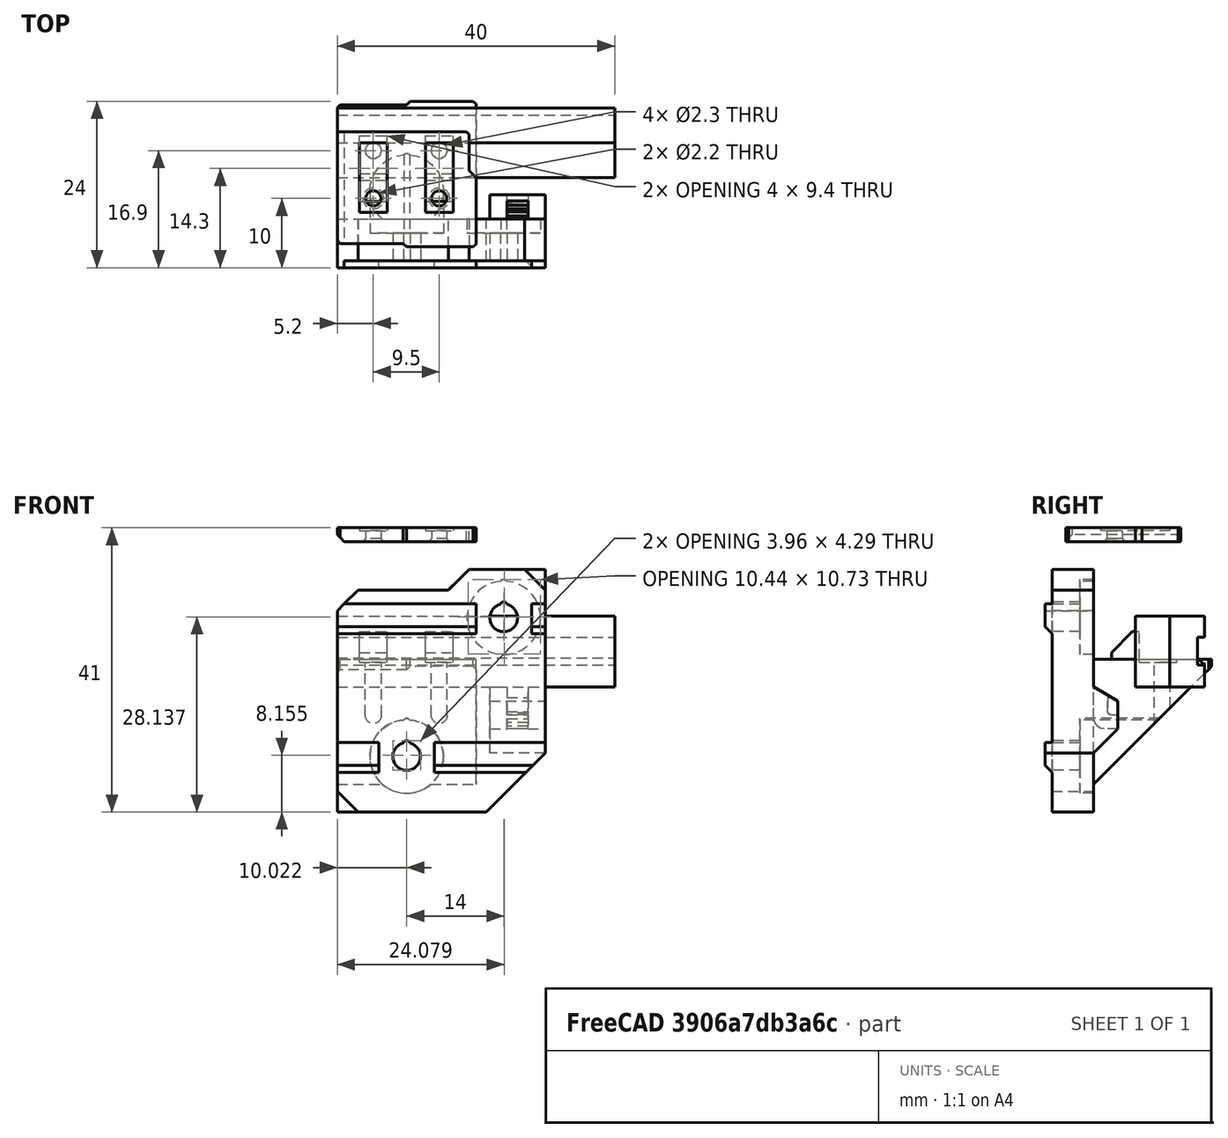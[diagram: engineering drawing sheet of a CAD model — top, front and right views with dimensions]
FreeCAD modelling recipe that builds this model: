
FCSTD DOCUMENT  (FreeCAD 0.18R14555 (Git shallow))
Label: Y-end-stop
License: All rights reserved
LicenseURL: http://en.wikipedia.org/wiki/All_rights_reserved
objects: Part::Cut×21, Part::Box×18, Part::Cylinder×14, Part::Chamfer×12, Part::MultiFuse×11, Part::Feature×10, App::DocumentObjectGroup×1
note: 86 computed .brp shape members not serialized (recipe doc carries the construction recipe); baked Part::Feature solids carry a one-line shape summary decoded from their .brp

FEATURE [Part::Cylinder] Cylinder
  Angle = 360
  AttacherType = Attacher::AttachEngine3D
  Height = 10
  Placement = pos=(5.2,2.9,0) rot=(0,0,1;0rad)
  Radius = 0.9
FEATURE [Part::Cylinder] Cylinder001
  Angle = 360
  AttacherType = Attacher::AttachEngine3D
  Height = 10
  Placement = pos=(14.7,2.9,0) rot=(0,0,1;0rad)
  Radius = 0.9
FEATURE [Part::Box] Box  label="Cube"
  AttacherType = Attacher::AttachEngine3D
  Height = 18
  Length = 10
  Placement = pos=(0,-7,-14) rot=(0,0,1;0rad)
  Width = 16.5
FEATURE [Part::Box] Box001  label="Cube001"
  AttacherType = Attacher::AttachEngine3D
  Height = 18
  Length = 10.5
  Placement = pos=(9.5,-7,-14) rot=(0,0,1;0rad)
  Width = 17
FEATURE [Part::Box] Box002  label="Cube002"
  AttacherType = Attacher::AttachEngine3D
  Height = 0.4
  Length = 4
  Placement = pos=(3.2,-0.4,3.6) rot=(0,0,1;0rad)
  Width = 5.4
FEATURE [Part::Box] Box003  label="Cube003"
  AttacherType = Attacher::AttachEngine3D
  Height = 0.4
  Length = 4
  Placement = pos=(12.7,-0.4,3.6) rot=(0,0,1;0rad)
  Width = 5.4
FEATURE [Part::Box] Box007  label="Cube007"
  AttacherType = Attacher::AttachEngine3D
  Height = 35
  Length = 30
  Placement = pos=(0,-12,-18) rot=(0,0,1;0rad)
  Width = 6
FEATURE [Part::MultiFuse] Fusion003
  Shapes = -> [Box003,Box002]
FEATURE [Part::Cylinder] Cylinder002
  Angle = 360
  AttacherType = Attacher::AttachEngine3D
  Height = 16
  Placement = pos=(10,9,-10) rot=(1,0,0;1.5708rad)
  Radius = 5.3
FEATURE [Part::Chamfer] Chamfer
  Base = -> Box001
  Edges = 1 edges r=1: [Edge3]
FEATURE [Part::Chamfer] Chamfer003
  Base = -> Box
  Edges = 1 edges r=0.4: [Edge3]
FEATURE [Part::Chamfer] Chamfer004
  Base = -> Chamfer
  Edges = 1 edges r=0.4: [Edge15]
FEATURE [Part::MultiFuse] Fusion
  Shapes = -> [Chamfer004,Chamfer003]
FEATURE [Part::Cut] Cut
  Base = -> Fusion
  Tool = -> Fusion003
FEATURE [Part::Feature] Body001
  Placement = pos=(0,-7,5) rot=(0,0,1;0rad)
  shape: bbox 20 x 19 x 19 mm, 5 faces (baked)
FEATURE [Part::Feature] Part__Feature  label="Common002"
  Placement = pos=(44.5,56.745,-30) rot=(0,0,1;3.14159rad)
  shape: bbox 8 x 3.5 x 9.5 mm, 30 faces (baked)
FEATURE [Part::Cylinder] Cylinder004
  Angle = 360
  AttacherType = Attacher::AttachEngine3D
  Height = 16
  Placement = pos=(24,9,10) rot=(1,0,0;1.5708rad)
  Radius = 5.3
FEATURE [Part::Feature] Fusion008001  label="Fusion009"
  shape: bbox 30 x 1.4 x 8.45 mm, 8 faces (baked)
FEATURE [Part::Feature] Fusion008002  label="Fusion010"
  Placement = pos=(0,0,20) rot=(0,0,1;0rad)
  shape: bbox 30 x 1.4 x 8.45 mm, 8 faces (baked)
FEATURE [Part::MultiFuse] Fusion008005
  Placement = pos=(0,0,-5) rot=(0,0,1;0rad)
  Shapes = -> [Cylinder001,Cylinder]
FEATURE [Part::Cylinder] Cylinder005
  Angle = 360
  AttacherType = Attacher::AttachEngine3D
  Height = 25
  Placement = pos=(24,9,10) rot=(1,0,0;1.5708rad)
  Radius = 2
FEATURE [Part::Cylinder] Cylinder006
  Angle = 360
  AttacherType = Attacher::AttachEngine3D
  Height = 25
  Placement = pos=(10,9,-10) rot=(1,0,0;1.5708rad)
  Radius = 2
FEATURE [Part::Cylinder] Cylinder007
  Angle = 360
  AttacherType = Attacher::AttachEngine3D
  Height = 25
  Placement = pos=(24,9,11.8) rot=(1,0,0;1.5708rad)
  Radius = 0.5
FEATURE [Part::Cylinder] Cylinder008
  Angle = 360
  AttacherType = Attacher::AttachEngine3D
  Height = 25
  Placement = pos=(10,9,-8.2) rot=(1,0,0;1.5708rad)
  Radius = 0.5
FEATURE [Part::Cylinder] Cylinder009
  Angle = 360
  AttacherType = Attacher::AttachEngine3D
  Height = 16
  Placement = pos=(24,8,15) rot=(1,0,0;1.5708rad)
  Radius = 0.5
FEATURE [Part::Cylinder] Cylinder010
  Angle = 360
  AttacherType = Attacher::AttachEngine3D
  Height = 16
  Placement = pos=(10,8,-5) rot=(1,0,0;1.5708rad)
  Radius = 0.5
FEATURE [Part::Feature] Chamfer002001  label="Chamfer009"
  Placement = pos=(0,1,-2) rot=(0,0,1;0rad)
  shape: bbox 4 x 4 x 6 mm, 7 faces (baked)
FEATURE [Part::Feature] Chamfer001001  label="Chamfer010"
  Placement = pos=(0,1,-2) rot=(0,0,1;0rad)
  shape: bbox 4 x 4 x 6 mm, 7 faces (baked)
FEATURE [Part::Cut] Cut001
  Base = -> Cut
  Tool = -> Body001
FEATURE [Part::Cut] Cut002
  Base = -> Cut001
  Placement = pos=(0,1,0) rot=(0,0,1;0rad)
  Tool = -> Fusion008005
FEATURE [Part::Box] Box012  label="Cube012"
  AttacherType = Attacher::AttachEngine3D
  Height = 10
  Length = 22
  Width = 10
FEATURE [Part::Box] Box013  label="Cube013"
  AttacherType = Attacher::AttachEngine3D
  Height = 14
  Length = 14
  Placement = pos=(28,-15,-29) rot=(0,0,1;0rad)
  Width = 14
FEATURE [Part::Chamfer] Chamfer006004
  Base = -> Box013
  Edges = 1 edges r=9: [Edge2]
  Placement = pos=(-7,0,5.5) rot=(0,0,1;0rad)
FEATURE [Part::Feature] Fusion008018001  label="Fusion008019"
  shape: bbox 20 x 17 x 2 mm, 10 faces (baked)
FEATURE [Part::Box] Box016  label="Cube016"
  AttacherType = Attacher::AttachEngine3D
  Height = 0.4
  Length = 4
  Placement = pos=(3.2,0,0) rot=(0,0,1;0rad)
  Width = 10
FEATURE [Part::Box] Box017  label="Cube017"
  AttacherType = Attacher::AttachEngine3D
  Height = 0.4
  Length = 4
  Placement = pos=(12.7,0,0) rot=(0,0,1;0rad)
  Width = 10
FEATURE [Part::MultiFuse] Fusion008018002
  Placement = pos=(0,-5,10) rot=(0,0,1;0rad)
  Shapes = -> [Box017,Box016]
FEATURE [Part::Cut] Cut007
  Base = -> Fusion008018001
  Tool = -> Fusion008018002
FEATURE [Part::Cylinder] Cylinder011
  Angle = 360
  AttacherType = Attacher::AttachEngine3D
  Height = 10
  Placement = pos=(5.2,3,0) rot=(0,0,1;0rad)
  Radius = 1.1
FEATURE [Part::Cylinder] Cylinder012
  Angle = 360
  AttacherType = Attacher::AttachEngine3D
  Height = 10
  Placement = pos=(14.7,3,0) rot=(0,0,1;0rad)
  Radius = 1.1
FEATURE [Part::MultiFuse] Fusion008018003
  Placement = pos=(0,0,5) rot=(0,0,1;0rad)
  Shapes = -> [Cylinder011,Cylinder012]
FEATURE [Part::Cut] Cut008
  Base = -> Cut007
  Tool = -> Fusion008018003
FEATURE [Part::Chamfer] Chamfer006012
  Base = -> Cut008
  Edges = 2 edges r=0.4: [Edge12,Edge13]
FEATURE [Part::Box] Box018  label="Cube018"
  AttacherType = Attacher::AttachEngine3D
  Height = 10
  Length = 20
  Placement = pos=(0,-16.6,7) rot=(0,0,1;0rad)
  Width = 10
FEATURE [Part::Cut] Cut009  label="lit"
  Base = -> Chamfer006012
  Tool = -> Box018
FEATURE [Part::Chamfer] Chamfer006013
  Base = -> Box012
  Edges = 1 edges r=5: [Edge8]
  Placement = pos=(-1,-14,14) rot=(0,0,1;0rad)
FEATURE [Part::Box] Box019  label="Cube019"
  AttacherType = Attacher::AttachEngine3D
  Height = 10
  Length = 10
  Placement = pos=(0,-15,14) rot=(0,0,1;0rad)
  Width = 10
FEATURE [Part::Chamfer] Chamfer006015
  Base = -> Box019
  Edges = 1 edges r=5: [Edge8]
  Placement = pos=(-6,0,-4) rot=(0,0,1;0rad)
FEATURE [Part::Chamfer] Chamfer006016
  Base = -> Cut009
  Edges = 1 edges r=1: [Edge8]
FEATURE [Part::Box] Box021  label="Cube021"
  AttacherType = Attacher::AttachEngine3D
  Height = 10
  Length = 10
  Placement = pos=(19,-13,2) rot=(0,0,1;0rad)
  Width = 10
FEATURE [Part::Chamfer] Chamfer006020
  Base = -> Box021
  Edges = 1 edges r=1: [Edge3]
  Placement = pos=(0,3,0) rot=(0,0,1;0rad)
FEATURE [Part::Cut] Cut013
  Base = -> Chamfer006016
  Tool = -> Chamfer006020
FEATURE [Part::Chamfer] Chamfer006021  label="top-cap"
  Base = -> Cut013
  Edges = 1 edges r=0.4: [Edge27]
  Placement = pos=(0,0,33) rot=(1,0,0;3.14159rad)
FEATURE [Part::MultiFuse] Fusion008018006006
  Shapes = -> [Box007,Fusion008001,Fusion008002,Part__Feature,Cut002,Chamfer001001,Chamfer002001]
FEATURE [Part::Cut] Cut019
  Base = -> Fusion008018006006
  Tool = -> Chamfer006004
FEATURE [Part::Cylinder] Cylinder019
  Angle = 360
  AttacherType = Attacher::AttachEngine3D
  Height = 15
  Placement = pos=(5.2,3.9,-6) rot=(0,0,1;0rad)
  Radius = 1.15
FEATURE [Part::Cylinder] Cylinder020
  Angle = 360
  AttacherType = Attacher::AttachEngine3D
  Height = 15
  Placement = pos=(14.7,3.9,-6) rot=(0,0,1;0rad)
  Radius = 1.15
FEATURE [Part::MultiFuse] Fusion008018006007
  Placement = pos=(0,0,-1) rot=(0,0,1;0rad)
  Shapes = -> [Cylinder020,Cylinder019]
FEATURE [App::DocumentObjectGroup] Group  label="Export"
  Group = -> [Chamfer006021]
FEATURE [Part::Box] Box022  label="Cube022"
  AttacherType = Attacher::AttachEngine3D
  Height = 10.25
  Length = 40
  Width = 10
FEATURE [Part::Box] Box023  label="Cube023"
  AttacherType = Attacher::AttachEngine3D
  Height = 4
  Length = 40
  Placement = pos=(0,9,3.225) rot=(0,0,1;0rad)
  Width = 2
FEATURE [Part::Box] Box024  label="Cube024"
  AttacherType = Attacher::AttachEngine3D
  Height = 4
  Length = 40
  Placement = pos=(0,9,3.225) rot=(0,0,1;0rad)
  Width = 1
FEATURE [Part::Box] Box025  label="Cube025"
  AttacherType = Attacher::AttachEngine3D
  Height = 10.25
  Length = 40
  Placement = pos=(0,5,0) rot=(0,0,1;0rad)
  Width = 5
FEATURE [Part::Cut] Cut025  label="T-slot-align-cut"
  Base = -> Box025
  Tool = -> Box024
FEATURE [Part::Chamfer] Chamfer006019005
  Base = -> Box023
  Edges = 1 edges r=1: [Edge9]
FEATURE [Part::Cut] Cut026  label="T-slot-vertical-align-cut"
  Base = -> Box022
  Tool = -> Chamfer006019005
FEATURE [Part::Box] Box026  label="Cube026"
  AttacherType = Attacher::AttachEngine3D
  Height = 8
  Length = 8
  Placement = pos=(20,-14,6) rot=(0,0,1;0rad)
  Width = 2
FEATURE [Part::Box] Box027  label="Cube027"
  AttacherType = Attacher::AttachEngine3D
  Height = 8
  Length = 8
  Placement = pos=(6,-14,-13) rot=(0,0,1;0rad)
  Width = 2
FEATURE [Part::MultiFuse] Fusion008011
  Placement = pos=(0,-1,0) rot=(0,0,1;0rad)
  Shapes = -> [Cylinder004,Cylinder002]
FEATURE [Part::Cut] Cut026003005
  Base = -> Cut019
  Tool = -> Fusion008011
FEATURE [Part::MultiFuse] Fusion008018006008
  Shapes = -> [Cylinder009,Cylinder010]
FEATURE [Part::Cut] Cut026003006
  Base = -> Cut026003005
  Tool = -> Fusion008018006008
FEATURE [Part::MultiFuse] Fusion008018006009
  Shapes = -> [Cylinder006,Cylinder008]
FEATURE [Part::MultiFuse] Fusion008018006010
  Shapes = -> [Cylinder005,Cylinder007]
FEATURE [Part::Cut] Cut026003007
  Base = -> Cut026003006
  Tool = -> Fusion008018006010
FEATURE [Part::Cut] Cut026003008
  Base = -> Cut026003007
  Tool = -> Fusion008018006009
FEATURE [Part::Feature] Part__Feature001  label="tslot-vertical-align"
  Placement = pos=(44,-12,4.78) rot=(0,0,1;3.14159rad)
  shape: bbox 60 x 5 x 10.45 mm, 10 faces (baked)
FEATURE [Part::Feature] Part__Feature002  label="tslot-vertical-align001"
  Placement = pos=(44,-12,-15.22) rot=(0,0,1;3.14159rad)
  shape: bbox 60 x 5 x 10.45 mm, 10 faces (baked)
FEATURE [Part::Cut] Cut026003009
  Base = -> Cut026003008
  Tool = -> Part__Feature001
FEATURE [Part::Cut] Cut026003010
  Base = -> Cut026003009
  Tool = -> Part__Feature002
FEATURE [Part::Cut] Cut026003011
  Base = -> Cut026003010
  Tool = -> Box026
FEATURE [Part::Cut] Cut026003012
  Base = -> Cut026003011
  Tool = -> Box027
FEATURE [Part::Cut] Cut026003013
  Base = -> Cut026003012
  Tool = -> Fusion008018006007
FEATURE [Part::Cut] Cut026003014
  Base = -> Cut026003013
  Tool = -> Chamfer006013
FEATURE [Part::Cut] Cut026003015
  Base = -> Cut026003014
  Tool = -> Chamfer006015
FEATURE [Part::Feature] Cut026003015001  label="Cut026003016"
  shape: bbox 30 x 24 x 35 mm, 94 faces (baked)
FEATURE [Part::Chamfer] Chamfer006019006
  Base = -> Cut026003015001
  Edges = 2 edges r=3: [Edge22,Edge135]
